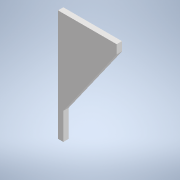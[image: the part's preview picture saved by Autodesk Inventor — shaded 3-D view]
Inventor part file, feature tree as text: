
AUTODESK INVENTOR PART (.ipt)
format: ipt  version: 2021 (Build 250183000, 183)  size: 94,720 bytes
history: native  units: in
note: dims shown in document units (in); Inventor stores cm internally (conversion verified against a paired STEP export)
features: extrude x1, sketch x1
ambient origin geometry x8: Origin, YZ Plane, XZ Plane, XY Plane, X Axis, Y Axis, Z Axis, Center Point
bodies: Solid1 (feature_tree)
feature tree (2):
  extrude  "Extrusion1"  Depth=0.5in
  sketch  "Sketch1"  dims[d1=0.5in d2=0.0in d3=0.5in d4=0.0344in]
